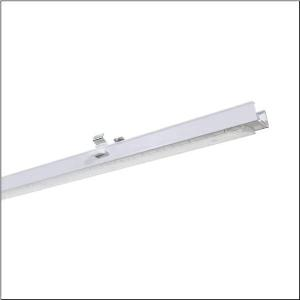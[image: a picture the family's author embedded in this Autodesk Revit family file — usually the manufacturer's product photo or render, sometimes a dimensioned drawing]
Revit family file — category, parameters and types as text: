
# Revit family: trunking_flex_31_51re11db4cb
name_source: partatom
category: Lighting Fixtures
units: mm (PartAtom-declared; Revit-internal decimal feet)

## family parameters
Cut with Voids When Loaded = No
Host = Face
Light Source = No
Part Type = Normal
Room Calculation Point = No
Round Connector Dimension = Use Diameter
Shared = No

## types (1)
- Trunking Flex 31 (1 x LED, 11500 lm, 66 W, 4000K)
    Apparent Load = 66 VA
    CIE Flux Codes = 83 93 98 100 100
    Color Rendering = 80
    Color Temperature = 4000K
    Default Elevation = 1800 mm
    Description = Trunking Flex 31, luminaire insert, of extruded aluminium section, coated, traffic white (RAL 9016), length: 1.472mm, width: 91mm, height: 53mm, LED rated luminous flux: 11.500lm, light colour: 840, control gear: DALI 2, with system connector: socket, mains connection: 220..240V, AC, 50/60Hz, rated input power: 66W, primary light control with lens, of plastic, primary optical cover: cover, of PMMA, light emission: direct distribution, protection rating (complete): IP20, insulation class (complete): insulation class I (protective earthing), certification: CE, UKCA, impact resistance: IK02, permissible ambient temperature for indoor applications: -20..+40°C, packaging unit: 1 piece
    Height = 58 mm
    Lamp = 1 x LED
    Lamp Light Flux = 11500 lm
    Lamp Power = 66 W
    Lamp count = 1
    Length = 1472 mm
    Luminous efficacy = 174 lm/W
    Manufacturer = Siteco
    ModVariant = No
    Model = 51RE11DB4CB
    Mounting Place = Ceiling
    Mounting Type = Pendant
    Number of Poles = 1
    OnlyDefault = Yes
    Power Factor = 1
    Product Name = Trunking Flex 31
    Product group = luminaire insert
    ProductGroupID = 901
    Protection Class = Protection class I
    Protection Degree = IP 20
    RLX_Detail_Level = 1
    RLX_Emergency_Light_Flux = 0 lm
    RLX_Emergency_Type = 0
    RLX_Emergency_Type_DB = No
    RlxData = <blob elided: 19437 chars, md5=004ebece>
    Socket = socket
    Standby Power = 0 W
    System Light Flux = 11500 lm
    System Power = 66 W
    Type Comments = Product without accessories
    Type Image = l_1266702.jpg
    URL = http://relux.com
    VarID = ---
    Voltage = 0 V
    Weight = 0.00 kg
    Width = 65 mm

## geometry (parser evidence)
native form markers: Blend x4, Sweep x12
no freeform markers — native parametric forms only
